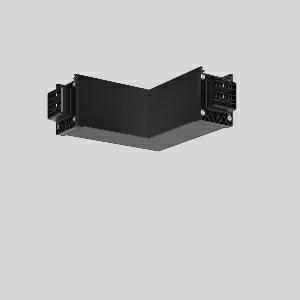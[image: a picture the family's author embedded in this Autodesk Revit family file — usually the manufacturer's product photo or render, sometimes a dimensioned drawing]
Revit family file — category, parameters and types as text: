
# Revit family: linedo_l-verbindung_982773_003_5_a57d
name_source: partatom
category: Lighting Fixtures
units: mm (PartAtom-declared; Revit-internal decimal feet)

## family parameters
Cut with Voids When Loaded = No
Host = Face
Light Source = No
Part Type = Normal
Room Calculation Point = No
Round Connector Dimension = Use Diameter
Shared = No

## types (1)
- LINEDO L-Verbindung
    Apparent Load = 0 VA
    Default Elevation = 1800 mm
    Description = Series: LINEDO
L-connector, 7-pole, connection plug / plug. Housing: extruded aluminium profile, powder-coated. Cover made of plastic, surface like housing. LINEDO plug system, plastic, black. Easy connection for rigid or flexible wires. 2 membrane cable entries (M25). Suitable for power supply in 7-pole version. Ready prewired. Colour-coded individual cables enable easy electromechanical separation.
Colour: jet black (RAL 9005)
Length: 204 mm
Width: 204 mm
Height: 76 mm
Weight: 640 g
    Height = 76 mm
    Lamp = 0 x
    Length = 204 mm
    Luminous efficacy = 0 lm/W
    Manufacturer = RZB
    ModVariant = No
    Model = 982773.003.5
    Mounting Place = Ceiling
    Mounting Type = Surface mounted
    Number of Poles = 1
    OnlyDefault = Yes
    Power Factor = 1
    Product Name = LINEDO L-Verbindung
    Product group = Surface mounted continuous line luminaire system
    ProductGroupID = 310
    Protection Class = Protection class I
    Protection Degree = Degree of protection
    RLX_Detail_Level = 1
    RLX_Emergency_Light_Flux = 0 lm
    RLX_Emergency_Type = 0
    RLX_Emergency_Type_DB = No
    RlxData = <blob elided: 19625 chars, md5=7db0a37d>
    Standby Power = 0 W
    System Light Flux = 0 lm
    System Power = 0 W
    Type Comments = Product without accessories
    Type Image = 982773.003.2.jpg
    URL = http://relux.com
    VarID = ---
    Voltage = 0 V
    Weight = 0.00 kg
    Width = 204 mm

## geometry (parser evidence)
native form markers: Blend x4, Sweep x11
no freeform markers — native parametric forms only
